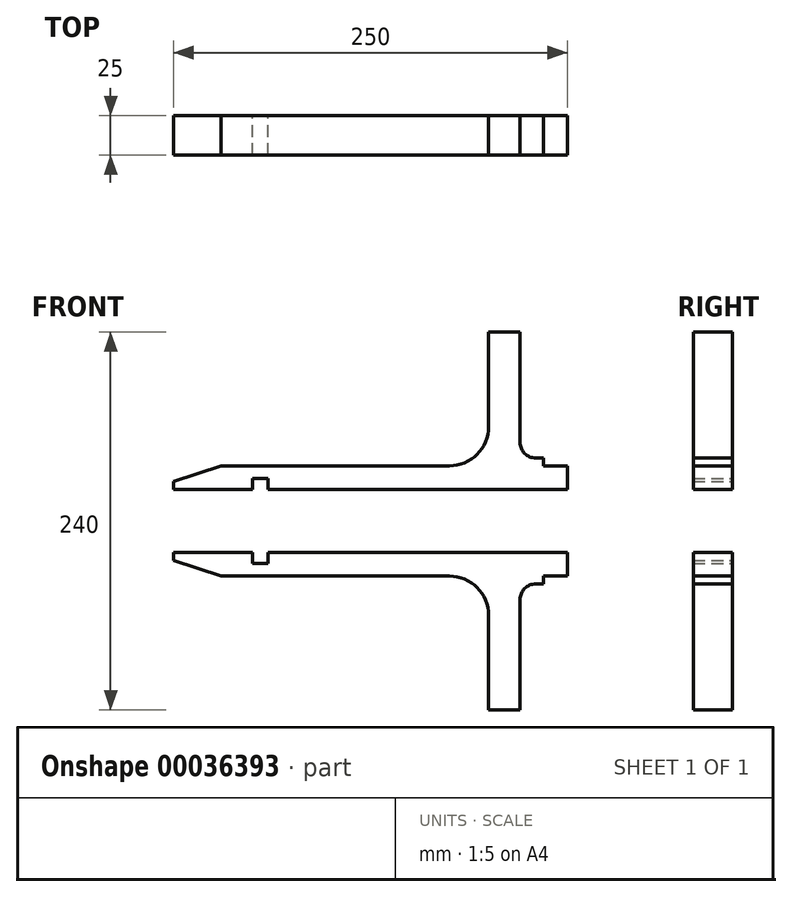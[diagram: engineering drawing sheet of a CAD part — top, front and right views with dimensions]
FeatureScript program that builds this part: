
annotation { "Feature Type Name" : "Feature", "Feature Type Description" : "" }
export const myFeature = defineFeature(function(context is Context, id is Id, definition is map)
    precondition{}
    {
        {
            var Q0;
            Q0=qCreatedBy(makeId("Front.planeOp"),FACE);
            var sketch = newSketch(context, id + "F0", { "sketchPlane" : qUnion([Q0])});
            skLineSegment(sketch, "E0", {"start": v(125, 20) * mm, "end": v(-65, 20) * mm});
            skLineSegment(sketch, "E1", {"start": v(-65, 20) * mm, "end": v(-65, 27) * mm});
            skLineSegment(sketch, "E2", {"start": v(-65, 27) * mm, "end": v(-75, 27) * mm});
            skLineSegment(sketch, "E3", {"start": v(-75, 27) * mm, "end": v(-75, 20) * mm});
            skLineSegment(sketch, "E4", {"start": v(-75, 20) * mm, "end": v(-125, 20) * mm});
            skLineSegment(sketch, "E5", {"start": v(-125, 20) * mm, "end": v(-125, 25) * mm});
            skLineSegment(sketch, "E6", {"start": v(-125, 25) * mm, "end": v(-95, 35) * mm});
            skLineSegment(sketch, "E7", {"start": v(-95, 35) * mm, "end": v(50, 35) * mm});
            skLineSegment(sketch, "E8", {"start": v(75, 60) * mm, "end": v(75, 120) * mm});
            skLineSegment(sketch, "E9", {"start": v(75, 120) * mm, "end": v(95, 120) * mm});
            skLineSegment(sketch, "E10", {"start": v(95, 120) * mm, "end": v(95, 50) * mm});
            skLineSegment(sketch, "E11", {"start": v(105, 40) * mm, "end": v(110, 40) * mm});
            skLineSegment(sketch, "E12", {"start": v(110, 40) * mm, "end": v(110, 35) * mm});
            skLineSegment(sketch, "E13", {"start": v(110, 35) * mm, "end": v(125, 35) * mm});
            skLineSegment(sketch, "E14", {"start": v(125, 35) * mm, "end": v(125, 20) * mm});
            skPoint(sketch, "E15.visualSharp", {"position": v(75, 35) * mm});
            skArc(sketch, "E15.filletArc", {"start": v(50, 35) * mm, "mid": v(67.68, 42.32) * mm, "end": v(75, 60) * mm});
            skPoint(sketch, "E16.visualSharp", {"position": v(95, 40) * mm});
            skArc(sketch, "E16.filletArc", {"start": v(95, 50) * mm, "mid": v(97.93, 42.93) * mm, "end": v(105, 40) * mm});
            skLineSegment(sketch, "E17.MirrorCS", {"start": v(105, -40) * mm, "end": v(110, -40) * mm});
            skLineSegment(sketch, "E18.MirrorCS", {"start": v(110, -40) * mm, "end": v(110, -35) * mm});
            skLineSegment(sketch, "E19.MirrorCS", {"start": v(-65, -20) * mm, "end": v(-65, -27) * mm});
            skLineSegment(sketch, "E20.MirrorCS", {"start": v(-75, -27) * mm, "end": v(-75, -20) * mm});
            skLineSegment(sketch, "E21.MirrorCS", {"start": v(-125, -20) * mm, "end": v(-125, -25) * mm});
            skArc(sketch, "E22.MirrorCS", {"start": v(95, -50) * mm, "mid": v(97.93, -42.93) * mm, "end": v(105, -40) * mm});
            skLineSegment(sketch, "E23.MirrorCS", {"start": v(125, -35) * mm, "end": v(125, -20) * mm});
            skLineSegment(sketch, "E24.MirrorCS", {"start": v(-95, -35) * mm, "end": v(50, -35) * mm});
            skLineSegment(sketch, "E25.MirrorCS", {"start": v(75, -120) * mm, "end": v(95, -120) * mm});
            skLineSegment(sketch, "E26.MirrorCS", {"start": v(-125, -25) * mm, "end": v(-95, -35) * mm});
            skLineSegment(sketch, "E27.MirrorCS", {"start": v(75, -60) * mm, "end": v(75, -120) * mm});
            skLineSegment(sketch, "E28.MirrorCS", {"start": v(110, -35) * mm, "end": v(125, -35) * mm});
            skPoint(sketch, "E29.MirrorP", {"position": v(75, -35) * mm});
            skArc(sketch, "E30.MirrorCS", {"start": v(50, -35) * mm, "mid": v(67.68, -42.32) * mm, "end": v(75, -60) * mm});
            skLineSegment(sketch, "E31.MirrorCS", {"start": v(-65, -27) * mm, "end": v(-75, -27) * mm});
            skLineSegment(sketch, "E32.MirrorCS", {"start": v(-75, -20) * mm, "end": v(-125, -20) * mm});
            skLineSegment(sketch, "E33.MirrorCS", {"start": v(125, -20) * mm, "end": v(-65, -20) * mm});
            skLineSegment(sketch, "E34.MirrorCS", {"start": v(95, -120) * mm, "end": v(95, -50) * mm});
            skPoint(sketch, "E35.MirrorP", {"position": v(95, -40) * mm});
            skSolve(sketch);
        }
        {
            var Q0;
            Q0=makeQuery(id+"F0.imprint","IMPRINT",FACE,{"disambiguationData":[TD([[makeQuery(id+"F0.imprint","IMPRINT",EDGE,{"derivedFrom":sQuery(id+"F0.wireOp",EDGE,"E0")}),-1.0]])]});
            var Q1;
            Q1=makeQuery(id+"F0.imprint","IMPRINT",FACE,{"disambiguationData":[TD([[makeQuery(id+"F0.imprint","IMPRINT",EDGE,{"derivedFrom":sQuery(id+"F0.wireOp",EDGE,"E17.MirrorCS")}),1.0]])]});
            extrude(context, id + "F1", {"entities" : qUnion([Q0, Q1]), "depth" : 25 * mm});
        }
    });
